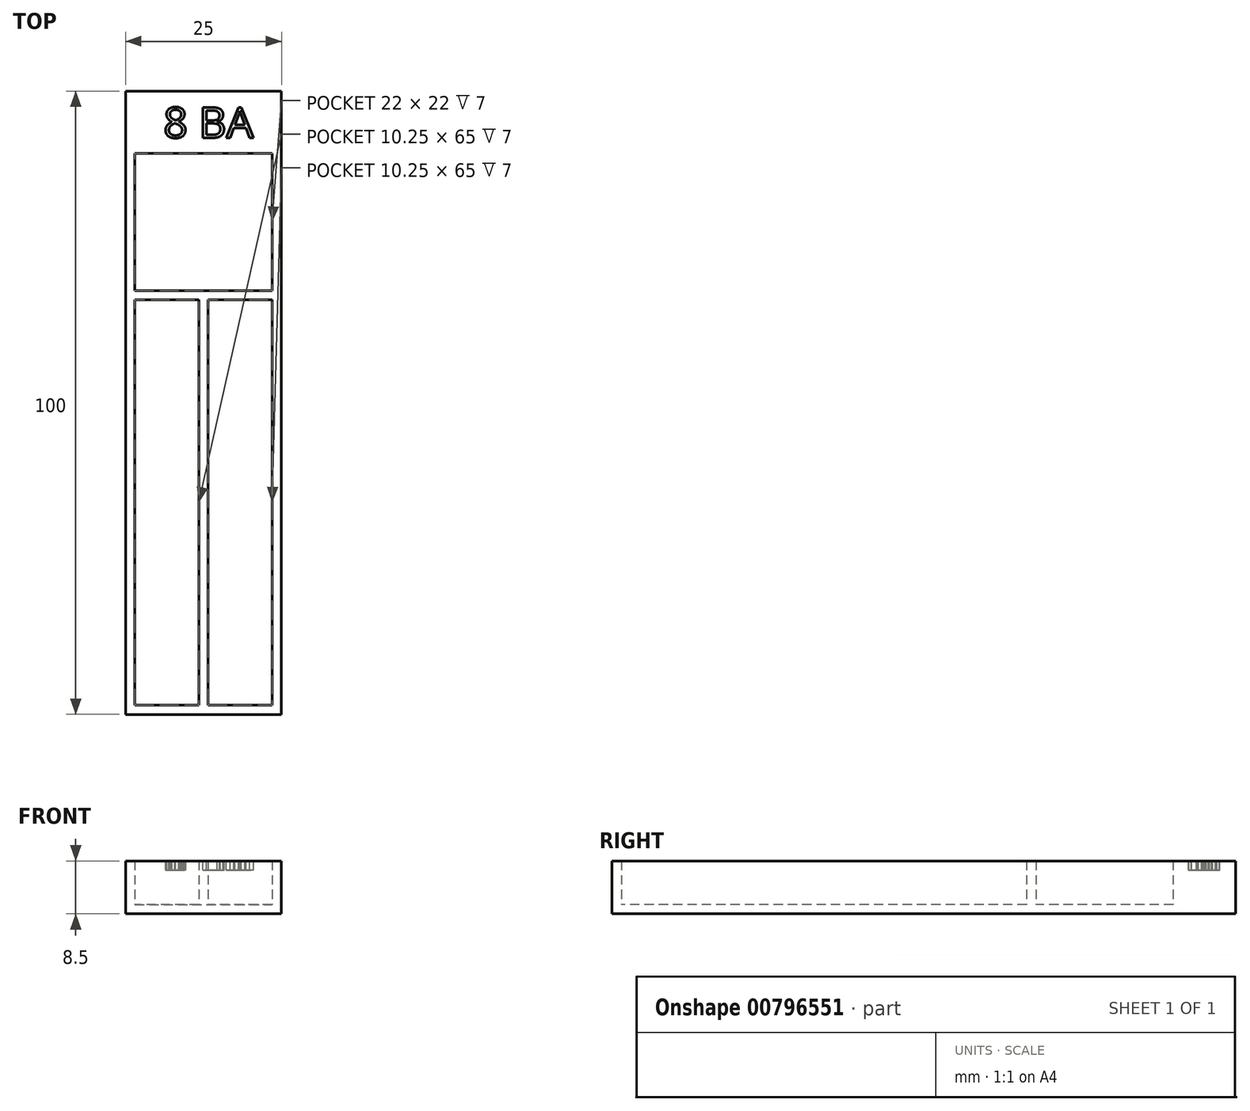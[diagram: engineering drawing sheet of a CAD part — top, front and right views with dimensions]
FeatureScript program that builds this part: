
annotation { "Feature Type Name" : "Feature", "Feature Type Description" : "" }
export const myFeature = defineFeature(function(context is Context, id is Id, definition is map)
    precondition{}
    {
        {
            var Q0;
            Q0=qCreatedBy(makeId("Top.planeOp"),FACE);
            var sketch = newSketch(context, id + "F0", { "sketchPlane" : qUnion([Q0])});
            skLineSegment(sketch, "E0.bottom", {"start": v(-4.34, 82.1) * mm, "end": v(20.66, 82.1) * mm});
            skLineSegment(sketch, "E0.top", {"start": v(-4.34, -17.9) * mm, "end": v(20.66, -17.9) * mm});
            skLineSegment(sketch, "E0.left", {"start": v(-4.34, 82.1) * mm, "end": v(-4.34, -17.9) * mm});
            skLineSegment(sketch, "E0.right", {"start": v(20.66, 82.1) * mm, "end": v(20.66, -17.9) * mm});
            skSolve(sketch);
        }
        {
            var Q0;
            Q0=makeQuery(id+"F0.imprint","IMPRINT",FACE,{"disambiguationData":[TD([[makeQuery(id+"F0.imprint","IMPRINT",EDGE,{"derivedFrom":sQuery(id+"F0.wireOp",EDGE,"E0.bottom")}),-1.0]])]});
            extrude(context, id + "F1", {"entities" : qUnion([Q0]), "endBound" : BoundingType.SYMMETRIC, "depth" : 1.5 * mm, "offsetDistance" : 25 * mm});
        }
        {
            var Q0;
            Q0=makeQuery(id+"F1.opExtrude","CAP_FACE",FACE,{"disambiguationData":[OSD([sQuery(id+"F0.wireOp",EDGE,"E0.bottom"),sQuery(id+"F0.wireOp",EDGE,"E0.top"),sQuery(id+"F0.wireOp",EDGE,"E0.left"),sQuery(id+"F0.wireOp",EDGE,"E0.right")])],"isStart":false});
            var sketch = newSketch(context, id + "F2", { "sketchPlane" : qUnion([Q0])});
            skLineSegment(sketch, "E1", {"start": v(8.16, 82.1) * mm, "end": v(8.16, -17.9) * mm, "construction": true});
            skLineSegment(sketch, "E2", {"start": v(2.66, -17.9) * mm, "end": v(4.66, -17.9) * mm});
            skLineSegment(sketch, "E3", {"start": v(2.66, 82.1) * mm, "end": v(2.66, 82.1) * mm});
            skLineSegment(sketch, "E4", {"start": v(-2.84, 72.1) * mm, "end": v(19.16, 72.1) * mm});
            skLineSegment(sketch, "E5", {"start": v(19.16, 72.1) * mm, "end": v(19.16, -16.4) * mm});
            skLineSegment(sketch, "E6", {"start": v(19.16, -16.4) * mm, "end": v(-2.84, -16.4) * mm});
            skLineSegment(sketch, "E7", {"start": v(-2.84, -16.4) * mm, "end": v(-2.84, 72.1) * mm});
            skLineSegment(sketch, "E8", {"start": v(-14.94, 32.1) * mm, "end": v(23.98, 32.1) * mm, "construction": true});
            skPoint(sketch, "E8.startSnap0", {"position": v(-4.34, 32.1) * mm});
            skLineSegment(sketch, "E9", {"start": v(-2.84, 50.1) * mm, "end": v(19.16, 50.1) * mm});
            skLineSegment(sketch, "E10", {"start": v(19.16, 50.1) * mm, "end": v(19.16, 48.6) * mm});
            skLineSegment(sketch, "E11", {"start": v(19.16, 48.6) * mm, "end": v(-2.84, 48.6) * mm});
            skLineSegment(sketch, "E12", {"start": v(-2.84, 48.6) * mm, "end": v(-2.84, 50.1) * mm});
            skLineSegment(sketch, "E13", {"start": v(7.4, 48.6) * mm, "end": v(7.4, -16.4) * mm});
            skLineSegment(sketch, "E14", {"start": v(7.4, -16.4) * mm, "end": v(8.9, -16.4) * mm});
            skLineSegment(sketch, "E15", {"start": v(8.9, -16.4) * mm, "end": v(8.9, 48.6) * mm});
            skLineSegment(sketch, "E16", {"start": v(8.9, 48.6) * mm, "end": v(7.4, 48.6) * mm});
            skSolve(sketch);
        }
        {
            var Q0;
            {var subQ11=sQuery(id+"F2.wireOp",EDGE,"E2");Q0=makeQuery(id+"F2.imprint","IMPRINT",FACE,{"disambiguationData":[TD([[makeQuery(id+"F2.imprint","IMPRINT",EDGE,{"derivedFrom":subQ11}),1.0]])]});}
            var Q1;
            Q1=makeQuery(id+"F2.imprint","IMPRINT",FACE,{"disambiguationData":[TD([[makeQuery(id+"F2.imprint","IMPRINT",EDGE,{"derivedFrom":sQuery(id+"F2.wireOp",EDGE,"E9")}),-1.0]])]});
            var Q2;
            Q2=makeQuery(id+"F2.imprint","IMPRINT",FACE,{"disambiguationData":[TD([[makeQuery(id+"F2.imprint","IMPRINT",EDGE,{"derivedFrom":sQuery(id+"F2.wireOp",EDGE,"E13")}),1.0]])]});
            extrude(context, id + "F3", {"entities" : qUnion([Q0, Q1, Q2]), "operationType" : NewBodyOperationType.ADD, "depth" : 7 * mm, "offsetDistance" : 25 * mm});
        }
        {
            var Q0;
            Q0=makeQuery(id+"F3.opExtrude","CAP_FACE",FACE,{"disambiguationData":[OSD([sQuery(id+"F0.wireOp",EDGE,"E0.bottom"),sQuery(id+"F0.wireOp",EDGE,"E0.top"),sQuery(id+"F0.wireOp",EDGE,"E0.left"),sQuery(id+"F0.wireOp",EDGE,"E0.right"),sQuery(id+"F2.wireOp",EDGE,"E2"),sQuery(id+"F2.wireOp",EDGE,"E4"),sQuery(id+"F2.wireOp",EDGE,"E5"),sQuery(id+"F2.wireOp",EDGE,"E6"),sQuery(id+"F2.wireOp",EDGE,"E7"),sQuery(id+"F2.wireOp",EDGE,"E9"),sQuery(id+"F2.wireOp",EDGE,"E11"),sQuery(id+"F2.wireOp",EDGE,"E13"),sQuery(id+"F2.wireOp",EDGE,"E15")])],"isStart":false});
            var sketch = newSketch(context, id + "F4", { "sketchPlane" : qUnion([Q0])});
            skText(sketch, "E17", { "text": "8 BA", "fontName": "OpenSans-Regular.ttf"});
            const initialGuessF4  = {"E17": [0.00172, 0.0746, 1, 0, 0.00492]};
            skSetInitialGuess(sketch, initialGuessF4);
            skSolve(sketch);
        }
        {
            var Q0;
            Q0=makeQuery(id+"F4.imprint","IMPRINT",FACE,{"disambiguationData":[TD([[makeQuery(id+"F4.imprint","IMPRINT",EDGE,{"derivedFrom":sQuery(id+"F4.wireOp",EDGE,"E17.sketch_text.stroke-0")}),-1.0]])]});
            var Q1;
            Q1=makeQuery(id+"F4.imprint","IMPRINT",FACE,{"disambiguationData":[TD([[makeQuery(id+"F4.imprint","IMPRINT",EDGE,{"derivedFrom":sQuery(id+"F4.wireOp",EDGE,"E17.sketch_text.stroke-16")}),-1.0]])]});
            var Q2;
            Q2=makeQuery(id+"F4.imprint","IMPRINT",FACE,{"disambiguationData":[TD([[makeQuery(id+"F4.imprint","IMPRINT",EDGE,{"derivedFrom":sQuery(id+"F4.wireOp",EDGE,"E17.sketch_text.stroke-41")}),-1.0]])]});
            var Q3;
            Q3=makeQuery(id+"F4.imprint","IMPRINT",FACE,{"disambiguationData":[TD([[makeQuery(id+"F4.imprint","IMPRINT",EDGE,{"derivedFrom":sQuery(id+"F4.wireOp",EDGE,"E17.sketch_text.stroke-50")}),-1.0]])]});
            var Q4;
            Q4=makeQuery(id+"F4.imprint","IMPRINT",FACE,{"disambiguationData":[TD([[makeQuery(id+"F4.imprint","IMPRINT",EDGE,{"derivedFrom":sQuery(id+"F4.wireOp",EDGE,"E17.sketch_text.stroke-56")}),-1.0]])]});
            extrude(context, id + "F5", {"entities" : qUnion([Q0, Q1, Q2, Q3, Q4]), "operationType" : NewBodyOperationType.REMOVE, "oppositeDirection" : true, "depth" : 1.5 * mm, "offsetDistance" : 25 * mm});
        }
    });
